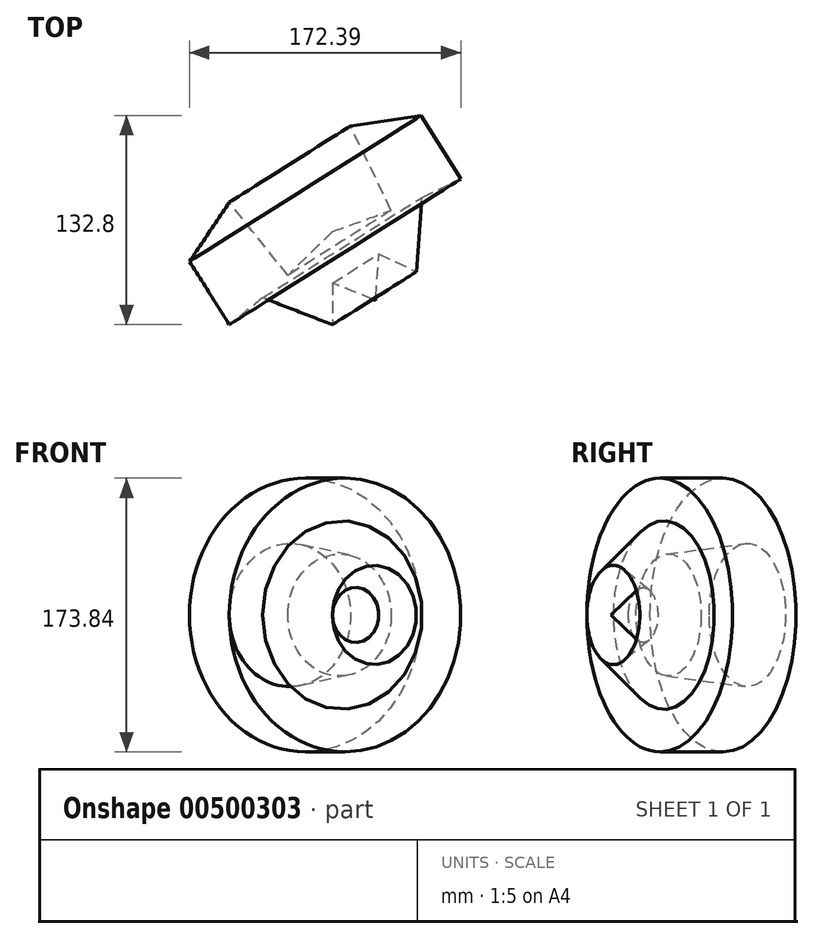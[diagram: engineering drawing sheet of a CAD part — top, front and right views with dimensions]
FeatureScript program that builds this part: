
annotation { "Feature Type Name" : "Feature", "Feature Type Description" : "" }
export const myFeature = defineFeature(function(context is Context, id is Id, definition is map)
    precondition{}
    {
        {
            var Q0;
            Q0=qCreatedBy(makeId("Top.planeOp"),FACE);
            var sketch = newSketch(context, id + "F0", { "sketchPlane" : qUnion([Q0])});
            skLineSegment(sketch, "E0", {"start": v(0, 0) * mm, "end": v(-37.2, 46.47) * mm});
            skLineSegment(sketch, "E1", {"start": v(-37.2, 46.47) * mm, "end": v(-62.5, 8.9) * mm});
            skLineSegment(sketch, "E2", {"start": v(-62.5, 8.9) * mm, "end": v(-37.2, -31.28) * mm});
            skLineSegment(sketch, "E3", {"start": v(-37.2, -31.28) * mm, "end": v(-16, -14.17) * mm});
            skLineSegment(sketch, "E4", {"start": v(0, 0) * mm, "end": v(28.27, 27.87) * mm});
            skLineSegment(sketch, "E5", {"start": v(28.27, 27.87) * mm, "end": v(55.79, -15.84) * mm});
            skLineSegment(sketch, "E6", {"start": v(55.79, -15.84) * mm, "end": v(28.27, -4.87) * mm});
            skLineSegment(sketch, "E7", {"start": v(-16, -14.17) * mm, "end": v(28.27, -31.28) * mm});
            skLineSegment(sketch, "E8", {"start": v(28.27, -4.87) * mm, "end": v(28.27, -31.28) * mm});
            skSolve(sketch);
        }
        {
            var Q0;
            Q0=makeQuery(id+"F0.imprint","IMPRINT",FACE,{"disambiguationData":[TD([[makeQuery(id+"F0.imprint","IMPRINT",EDGE,{"derivedFrom":sQuery(id+"F0.wireOp",EDGE,"E0")}),1.0]])]});
            var Q1;
            Q1=sQuery(id+"F0.wireOp",EDGE,"E5");
            revolve(context, id + "F1", {"entities" : qUnion([Q0]), "axis" : qUnion([Q1]), "revolveType" : RevolveType.FULL});
        }
    });
